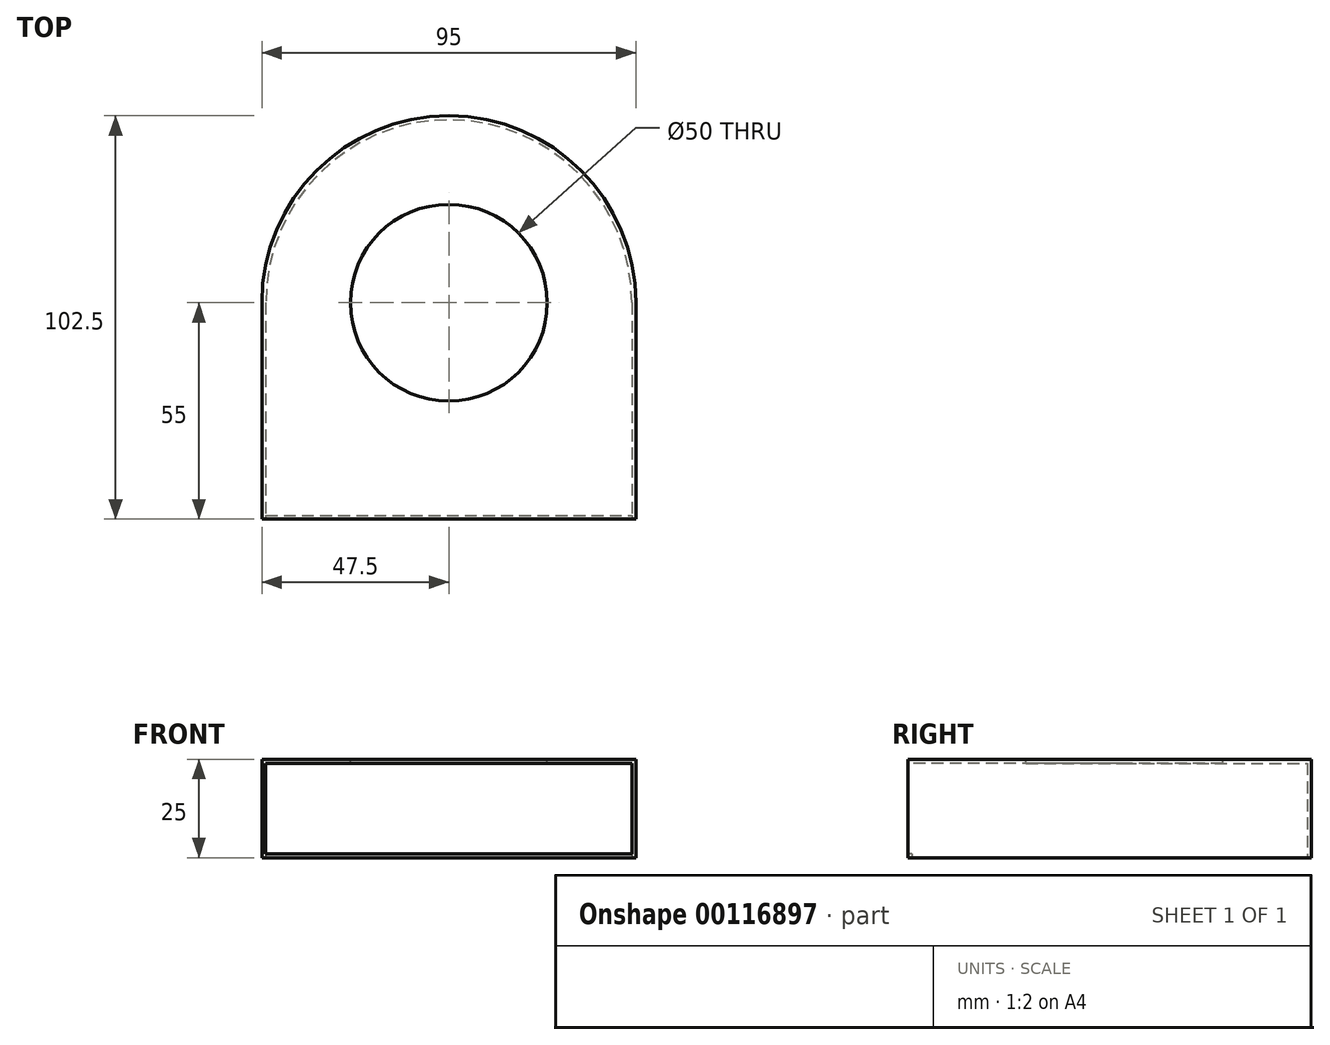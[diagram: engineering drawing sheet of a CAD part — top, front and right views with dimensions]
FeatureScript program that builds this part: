
annotation { "Feature Type Name" : "Feature", "Feature Type Description" : "" }
export const myFeature = defineFeature(function(context is Context, id is Id, definition is map)
    precondition{}
    {
        {
            var Q0;
            Q0=qCreatedBy(makeId("Top.planeOp"),FACE);
            var sketch = newSketch(context, id + "F0", { "sketchPlane" : qUnion([Q0])});
            skCircle(sketch, "E0", {"center": v(0, 0) * mm, "radius": 40 * mm, "construction": true});
            skCircle(sketch, "E1", {"center": v(0, 0) * mm, "radius": 47.5 * mm});
            skLineSegment(sketch, "E2", {"start": v(47.5, 29.87) * mm, "end": v(47.5, -69.76) * mm, "construction": true});
            skLineSegment(sketch, "E3.top", {"start": v(-47.5, -55) * mm, "end": v(47.5, -55) * mm});
            skLineSegment(sketch, "E3.left", {"start": v(-47.5, 0) * mm, "end": v(-47.5, -55) * mm});
            skLineSegment(sketch, "E3.right", {"start": v(47.5, 0) * mm, "end": v(47.5, -55) * mm});
            skSolve(sketch);
        }
        {
            var Q0;
            Q0 = qSketchRegion(id + "F0", true);
            extrude(context, id + "F1", {"entities" : qUnion([Q0]), "depth" : 25 * mm});
        }
        {
            var Q0;
            Q0=makeQuery(id+"F1.opExtrude","SWEPT_FACE",FACE,{"disambiguationData":[OSD([sQuery(id+"F0.wireOp",EDGE,"E3.top")])]});
            shell(context, id + "F2", {"entities" : qUnion([Q0]), "thickness" : 1 * mm});
        }
        {
            var Q0;
            Q0=makeQuery(id+"F1.opExtrude","CAP_FACE",FACE,{"disambiguationData":[OSD([sQuery(id+"F0.wireOp",EDGE,"E1"),sQuery(id+"F0.wireOp",EDGE,"E3.top"),sQuery(id+"F0.wireOp",EDGE,"E3.left"),sQuery(id+"F0.wireOp",EDGE,"E3.right")])],"isStart":false});
            var sketch = newSketch(context, id + "F3", { "sketchPlane" : qUnion([Q0])});
            skCircle(sketch, "E4", {"center": v(0, 0) * mm, "radius": 25 * mm});
            skSolve(sketch);
        }
        {
            var Q0;
            Q0 = qSketchRegion(id + "F3", true);
            extrude(context, id + "F4", {"entities" : qUnion([Q0]), "operationType" : NewBodyOperationType.REMOVE, "endBound" : BoundingType.THROUGH_ALL, "oppositeDirection" : true, "depth" : 21 * mm});
        }
        {
            var Q0;
            Q0=makeQuery(id+"F1.opExtrude","CAP_FACE",FACE,{"disambiguationData":[OSD([sQuery(id+"F0.wireOp",EDGE,"E1"),sQuery(id+"F0.wireOp",EDGE,"E3.top"),sQuery(id+"F0.wireOp",EDGE,"E3.left"),sQuery(id+"F0.wireOp",EDGE,"E3.right")])],"isStart":true});
            var sketch = newSketch(context, id + "F5", { "sketchPlane" : qUnion([Q0])});
            skLineSegment(sketch, "E5.0", {"start": v(-46.5, 0) * mm, "end": v(-46.5, 54) * mm});
            skArc(sketch, "E5.1", {"start": v(46.5, 0) * mm, "mid": v(0, -46.5) * mm, "end": v(-46.5, 0) * mm});
            skLineSegment(sketch, "E5.2", {"start": v(46.5, 0) * mm, "end": v(46.5, 54) * mm});
            skLineSegment(sketch, "E5.3", {"start": v(-46.5, 54) * mm, "end": v(46.5, 54) * mm});
            skSolve(sketch);
        }
        {
            var Q0;
            Q0 = qSketchRegion(id + "F5", true);
            var Q1;
            Q1=makeQuery(id+"F5.imprint","IMPRINT",FACE,{"disambiguationData":[TD([[makeQuery(id+"F5.imprint","IMPRINT",EDGE,{"derivedFrom":sQuery(id+"F5.wireOp",EDGE,"E5.0")}),-1.0]])]});
            extrude(context, id + "F6", {"entities" : qUnion([Q0, Q1]), "operationType" : NewBodyOperationType.REMOVE, "oppositeDirection" : true, "depth" : 2 * mm});
        }
    });
